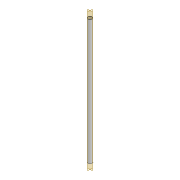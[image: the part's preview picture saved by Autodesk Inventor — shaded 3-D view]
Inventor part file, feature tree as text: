
AUTODESK INVENTOR PART (.ipt)
format: ipt  version: 2022 (Build 260153000, 153)  size: 76,800 bytes
history: native  units: mm
features: extrude x1, sketch x1
ambient origin geometry x8: Origin, YZ Plane, XZ Plane, XY Plane, X Axis, Y Axis, Z Axis, Center Point
bodies: Body1 (feature_tree)
feature tree (2):
  extrude  "Extrusion2"  Depth=350.0mm
  sketch  "Sketch2"  dims[d6=10.0mm d7=12.0mm d8=350.0mm d9=0.0mm]
